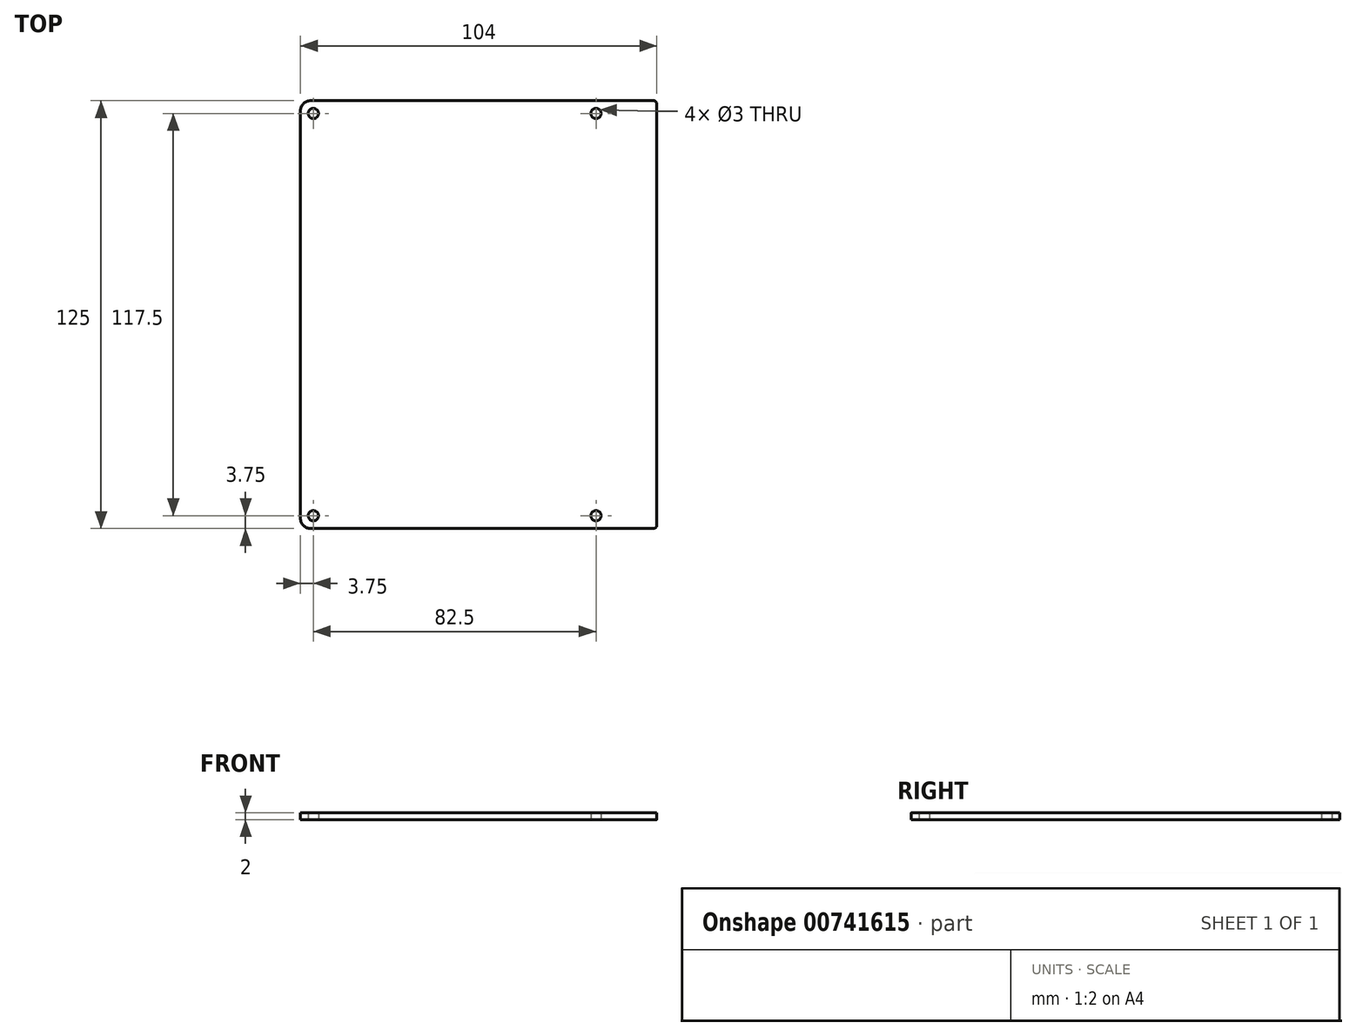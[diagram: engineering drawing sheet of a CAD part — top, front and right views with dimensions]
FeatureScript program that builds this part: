
annotation { "Feature Type Name" : "Feature", "Feature Type Description" : "" }
export const myFeature = defineFeature(function(context is Context, id is Id, definition is map)
    precondition{}
    {
        {
            var Q0;
            Q0=qCreatedBy(makeId("Top.planeOp"),FACE);
            var sketch = newSketch(context, id + "F0", { "sketchPlane" : qUnion([Q0])});
            skLineSegment(sketch, "E0.bottom", {"start": v(-49, 62.5) * mm, "end": v(51, 62.5) * mm});
            skLineSegment(sketch, "E0.top", {"start": v(-49, -62.5) * mm, "end": v(51, -62.5) * mm});
            skLineSegment(sketch, "E0.left", {"start": v(-52, 59.5) * mm, "end": v(-52, -59.5) * mm});
            skLineSegment(sketch, "E0.right", {"start": v(52, 61.5) * mm, "end": v(52, -61.5) * mm});
            skPoint(sketch, "E1.visualSharp", {"position": v(-52, 62.5) * mm});
            skArc(sketch, "E1.filletArc", {"start": v(-49, 62.5) * mm, "mid": v(-51.12, 61.62) * mm, "end": v(-52, 59.5) * mm});
            skPoint(sketch, "E2.visualSharp", {"position": v(-52, -62.5) * mm});
            skArc(sketch, "E2.filletArc", {"start": v(-52, -59.5) * mm, "mid": v(-51.12, -61.62) * mm, "end": v(-49, -62.5) * mm});
            skPoint(sketch, "E3.visualSharp", {"position": v(52, -62.5) * mm});
            skArc(sketch, "E3.filletArc", {"start": v(51, -62.5) * mm, "mid": v(51.7, -62.2) * mm, "end": v(52, -61.5) * mm});
            skPoint(sketch, "E4.visualSharp", {"position": v(52, 62.5) * mm});
            skArc(sketch, "E4.filletArc", {"start": v(52, 61.5) * mm, "mid": v(51.7, 62.2) * mm, "end": v(51, 62.5) * mm});
            skCircle(sketch, "E5", {"center": v(-48.25, 58.75) * mm, "radius": 1.5 * mm});
            skCircle(sketch, "E6", {"center": v(34.25, 58.75) * mm, "radius": 1.5 * mm});
            skCircle(sketch, "E7.MirrorC", {"center": v(-48.25, -58.75) * mm, "radius": 1.5 * mm});
            skCircle(sketch, "E8.MirrorC", {"center": v(34.25, -58.75) * mm, "radius": 1.5 * mm});
            skSolve(sketch);
        }
        {
            var Q0;
            Q0=makeQuery(id+"F0.imprint","IMPRINT",FACE,{"disambiguationData":[TD([[makeQuery(id+"F0.imprint","IMPRINT",EDGE,{"derivedFrom":sQuery(id+"F0.wireOp",EDGE,"E0.bottom")}),-1.0]])]});
            extrude(context, id + "F1", {"entities" : qUnion([Q0]), "depth" : 2 * mm, "offsetDistance" : 25 * mm});
        }
    });
